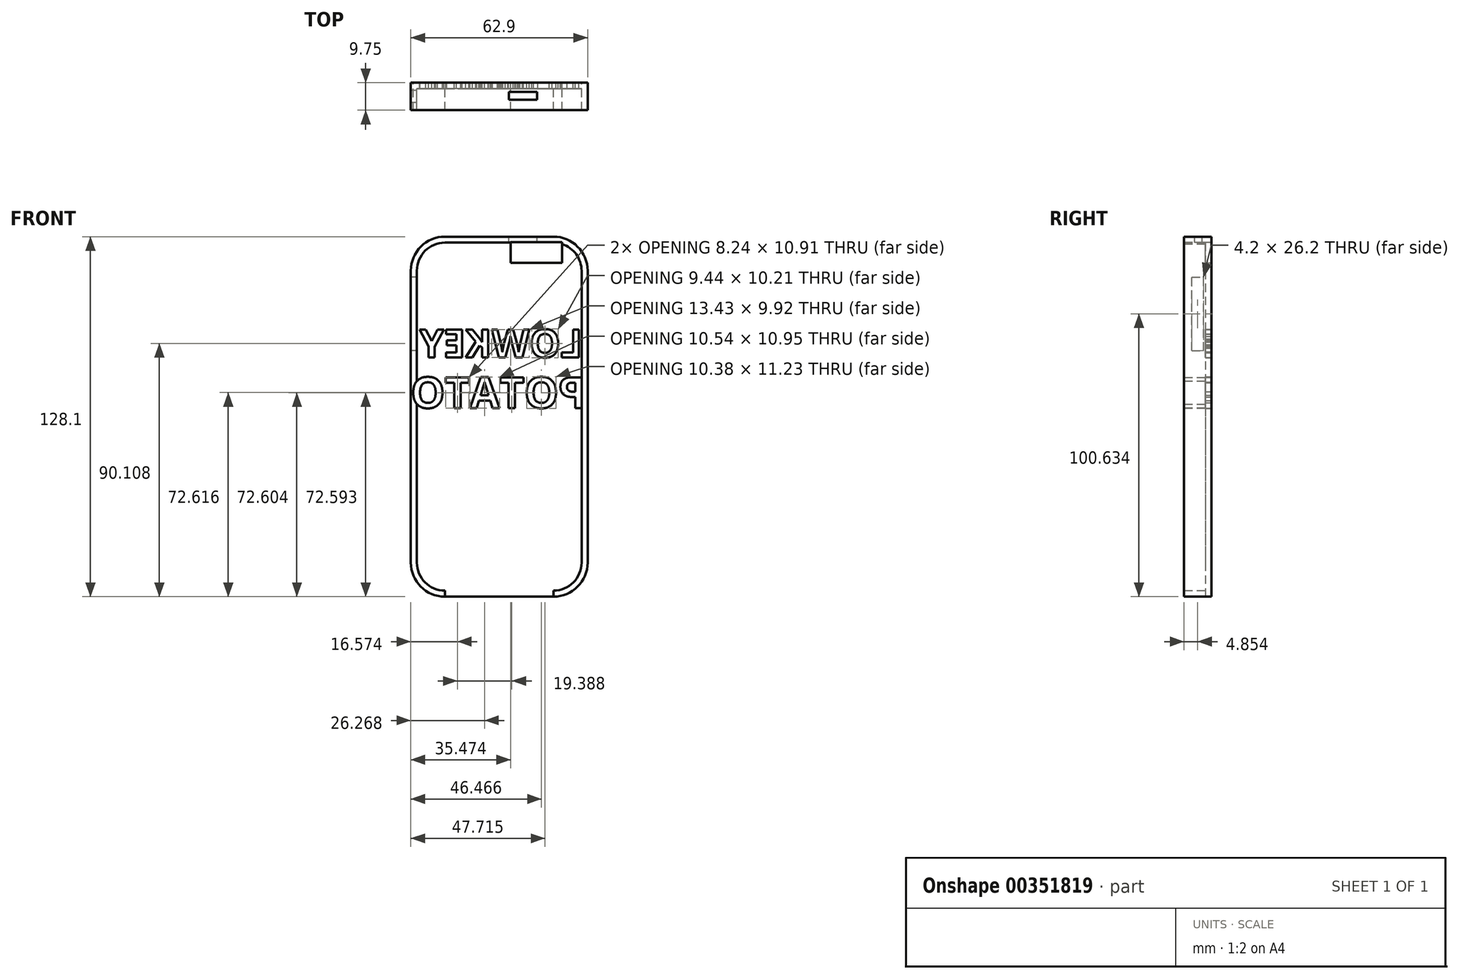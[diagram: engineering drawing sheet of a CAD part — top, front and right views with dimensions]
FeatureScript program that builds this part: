
annotation { "Feature Type Name" : "Feature", "Feature Type Description" : "" }
export const myFeature = defineFeature(function(context is Context, id is Id, definition is map)
    precondition{}
    {
        {
            var Q0;
            Q0=qCreatedBy(makeId("Front.planeOp"),FACE);
            var sketch = newSketch(context, id + "F0", { "sketchPlane" : qUnion([Q0])});
            skLineSegment(sketch, "E0.bottom", {"start": v(-28.32, 63.18) * mm, "end": v(10.28, 63.18) * mm});
            skLineSegment(sketch, "E0.top", {"start": v(-28.32, -60.62) * mm, "end": v(10.28, -60.62) * mm});
            skLineSegment(sketch, "E0.left", {"start": v(-38.32, 53.18) * mm, "end": v(-38.32, -50.62) * mm});
            skLineSegment(sketch, "E0.right", {"start": v(20.28, 53.18) * mm, "end": v(20.28, -50.62) * mm});
            skPoint(sketch, "E1.visualSharp", {"position": v(-38.32, 63.18) * mm});
            skArc(sketch, "E1.filletArc", {"start": v(-28.32, 63.18) * mm, "mid": v(-35.39, 60.26) * mm, "end": v(-38.32, 53.18) * mm});
            skPoint(sketch, "E2.visualSharp", {"position": v(-38.32, -60.62) * mm});
            skArc(sketch, "E2.filletArc", {"start": v(-38.32, -50.62) * mm, "mid": v(-35.39, -57.69) * mm, "end": v(-28.32, -60.62) * mm});
            skPoint(sketch, "E3.visualSharp", {"position": v(20.28, 63.18) * mm});
            skArc(sketch, "E3.filletArc", {"start": v(20.28, 53.18) * mm, "mid": v(17.35, 60.26) * mm, "end": v(10.28, 63.18) * mm});
            skPoint(sketch, "E4.visualSharp", {"position": v(20.28, -60.62) * mm});
            skArc(sketch, "E4.filletArc", {"start": v(10.28, -60.62) * mm, "mid": v(17.35, -57.69) * mm, "end": v(20.28, -50.62) * mm});
            skLineSegment(sketch, "E5", {"start": v(-38.32, 53.18) * mm, "end": v(20.28, 53.18) * mm});
            skSolve(sketch);
        }
        {
            var Q0;
            Q0=makeQuery(id+"F0.imprint","IMPRINT",FACE,{"disambiguationData":[TD([[makeQuery(id+"F0.imprint","IMPRINT",EDGE,{"derivedFrom":sQuery(id+"F0.wireOp",EDGE,"E0.top")}),1.0]])]});
            var Q1;
            Q1=makeQuery(id+"F0.imprint","IMPRINT",FACE,{"disambiguationData":[TD([[makeQuery(id+"F0.imprint","IMPRINT",EDGE,{"derivedFrom":sQuery(id+"F0.wireOp",EDGE,"E0.bottom")}),-1.0]])]});
            extrude(context, id + "F1", {"entities" : qUnion([Q0, Q1]), "depth" : 7.6 * mm});
        }
        {
            var Q0;
            Q0=makeQuery(id+"F1.opExtrude","CAP_FACE",FACE,{"disambiguationData":[OSD([sQuery(id+"F0.wireOp",EDGE,"E0.bottom"),sQuery(id+"F0.wireOp",EDGE,"E0.top"),sQuery(id+"F0.wireOp",EDGE,"E0.left"),sQuery(id+"F0.wireOp",EDGE,"E0.right"),sQuery(id+"F0.wireOp",EDGE,"E1.filletArc"),sQuery(id+"F0.wireOp",EDGE,"E2.filletArc"),sQuery(id+"F0.wireOp",EDGE,"E3.filletArc"),sQuery(id+"F0.wireOp",EDGE,"E4.filletArc")])],"isStart":false});
            shell(context, id + "F2", {"entities" : qUnion([Q0]), "thickness" : 2.15 * mm, "oppositeDirection" : true});
        }
        {
            var Q0;
            Q0=makeQuery(id+"F1.opExtrude","SWEPT_FACE",FACE,{"disambiguationData":[OSD([sQuery(id+"F0.wireOp",EDGE,"E0.top")])]});
            var sketch = newSketch(context, id + "F3", { "sketchPlane" : qUnion([Q0])});
            skLineSegment(sketch, "E6", {"start": v(-28.32, 0) * mm, "end": v(10.28, 0) * mm});
            skSolve(sketch);
        }
        {
            var Q0;
            {var subQ0=sQuery(id+"F3.wireOp",EDGE,"E6");Q0=makeQuery(id+"F3.imprint","IMPRINT",FACE,{"disambiguationData":[TD([[makeQuery(id+"F3.imprint","IMPRINT",EDGE,{"derivedFrom":subQ0}),1.0]])]});}
            extrude(context, id + "F4", {"entities" : qUnion([Q0]), "operationType" : NewBodyOperationType.REMOVE, "oppositeDirection" : true, "depth" : 50.72 * mm});
        }
        {
            var Q0;
            Q0=makeQuery(id+"F1.opExtrude","CAP_FACE",FACE,{"disambiguationData":[OSD([sQuery(id+"F0.wireOp",EDGE,"E0.bottom"),sQuery(id+"F0.wireOp",EDGE,"E0.top"),sQuery(id+"F0.wireOp",EDGE,"E0.left"),sQuery(id+"F0.wireOp",EDGE,"E0.right"),sQuery(id+"F0.wireOp",EDGE,"E1.filletArc"),sQuery(id+"F0.wireOp",EDGE,"E2.filletArc"),sQuery(id+"F0.wireOp",EDGE,"E3.filletArc"),sQuery(id+"F0.wireOp",EDGE,"E4.filletArc")])],"isStart":true});
            var sketch = newSketch(context, id + "F5", { "sketchPlane" : qUnion([Q0])});
            skLineSegment(sketch, "E7", {"start": v(-22.43, 53.18) * mm, "end": v(40.47, 53.18) * mm});
            skLineSegment(sketch, "E8.bottom", {"start": v(-13.39, 63.4) * mm, "end": v(4.91, 63.4) * mm});
            skLineSegment(sketch, "E8.top", {"start": v(-13.39, 56) * mm, "end": v(4.91, 56) * mm});
            skLineSegment(sketch, "E8.left", {"start": v(-13.39, 63.4) * mm, "end": v(-13.39, 56) * mm});
            skLineSegment(sketch, "E8.right", {"start": v(4.91, 63.4) * mm, "end": v(4.91, 56) * mm});
            skSolve(sketch);
        }
        {
            var Q0;
            Q0=makeQuery(id+"F5.imprint","IMPRINT",FACE,{"disambiguationData":[TD([[makeQuery(id+"F5.imprint","IMPRINT",EDGE,{"derivedFrom":sQuery(id+"F5.wireOp",EDGE,"E8.bottom")}),-1.0]])]});
            extrude(context, id + "F6", {"entities" : qUnion([Q0]), "operationType" : NewBodyOperationType.REMOVE, "oppositeDirection" : true, "depth" : 18.3 * mm});
        }
        {
            var Q0;
            Q0=makeQuery(id+"F1.opExtrude","SWEPT_FACE",FACE,{"disambiguationData":[OSD([sQuery(id+"F0.wireOp",EDGE,"E0.left")])]});
            var sketch = newSketch(context, id + "F7", { "sketchPlane" : qUnion([Q0])});
            skLineSegment(sketch, "E9.bottom", {"start": v(0.65, 50.96) * mm, "end": v(4.85, 50.96) * mm});
            skLineSegment(sketch, "E9.top", {"start": v(0.65, 24.76) * mm, "end": v(4.85, 24.76) * mm});
            skLineSegment(sketch, "E9.left", {"start": v(0.65, 50.96) * mm, "end": v(0.65, 24.76) * mm});
            skLineSegment(sketch, "E9.right", {"start": v(4.85, 50.96) * mm, "end": v(4.85, 24.76) * mm});
            skSolve(sketch);
        }
        {
            var Q0;
            Q0=makeQuery(id+"F7.imprint","IMPRINT",FACE,{"disambiguationData":[TD([[makeQuery(id+"F7.imprint","IMPRINT",EDGE,{"derivedFrom":sQuery(id+"F7.wireOp",EDGE,"E9.bottom")}),-1.0]])]});
            extrude(context, id + "F8", {"entities" : qUnion([Q0]), "operationType" : NewBodyOperationType.REMOVE, "oppositeDirection" : true, "depth" : 26.6 * mm});
        }
        {
            var Q0;
            Q0=makeQuery(id+"F1.opExtrude","CAP_FACE",FACE,{"disambiguationData":[OSD([sQuery(id+"F0.wireOp",EDGE,"E0.bottom"),sQuery(id+"F0.wireOp",EDGE,"E0.top"),sQuery(id+"F0.wireOp",EDGE,"E0.left"),sQuery(id+"F0.wireOp",EDGE,"E0.right"),sQuery(id+"F0.wireOp",EDGE,"E1.filletArc"),sQuery(id+"F0.wireOp",EDGE,"E2.filletArc"),sQuery(id+"F0.wireOp",EDGE,"E3.filletArc"),sQuery(id+"F0.wireOp",EDGE,"E4.filletArc")])],"isStart":true});
            var sketch = newSketch(context, id + "F9", { "sketchPlane" : qUnion([Q0])});
            skPoint(sketch, "E10.startSnap0", {"position": v(-12.12, 0) * mm});
            skText(sketch, "E11", { "text": "LOWKEY", "fontName": "OpenSans-Bold.ttf"});
            skText(sketch, "E12", { "text": "POTATO", "fontName": "OpenSans-Bold.ttf"});
            const initialGuessF9  = {"E11": [-0.02062, 0.02237, 1, 0, 0.01], "E12": [-0.02167, 0.00437, 1, 0, 0.011]};
            skSetInitialGuess(sketch, initialGuessF9);
            skSolve(sketch);
        }
        {
            var Q0;
            Q0=makeQuery(id+"F1.opExtrude","SWEPT_FACE",FACE,{"disambiguationData":[OSD([sQuery(id+"F0.wireOp",EDGE,"E0.bottom")])]});
            var sketch = newSketch(context, id + "F10", { "sketchPlane" : qUnion([Q0])});
            skLineSegment(sketch, "E13.bottom", {"start": v(-5.54, -1.1) * mm, "end": v(4.46, -1.1) * mm});
            skLineSegment(sketch, "E13.top", {"start": v(-5.54, -3.85) * mm, "end": v(4.46, -3.85) * mm});
            skLineSegment(sketch, "E13.left", {"start": v(-5.54, -1.1) * mm, "end": v(-5.54, -3.85) * mm});
            skLineSegment(sketch, "E13.right", {"start": v(4.46, -1.1) * mm, "end": v(4.46, -3.85) * mm});
            skSolve(sketch);
        }
        {
            var Q0;
            Q0=makeQuery(id+"F10.imprint","IMPRINT",FACE,{"disambiguationData":[TD([[makeQuery(id+"F10.imprint","IMPRINT",EDGE,{"derivedFrom":sQuery(id+"F10.wireOp",EDGE,"E13.bottom")}),-1.0]])]});
            extrude(context, id + "F11", {"entities" : qUnion([Q0]), "operationType" : NewBodyOperationType.REMOVE, "oppositeDirection" : true, "depth" : 10 * mm});
        }
        {
            var Q0;
            Q0 = qSketchRegion(id + "F9", true);
            extrude(context, id + "F12", {"entities" : qUnion([Q0]), "operationType" : NewBodyOperationType.REMOVE, "oppositeDirection" : true, "depth" : 25 * mm});
        }
    });
